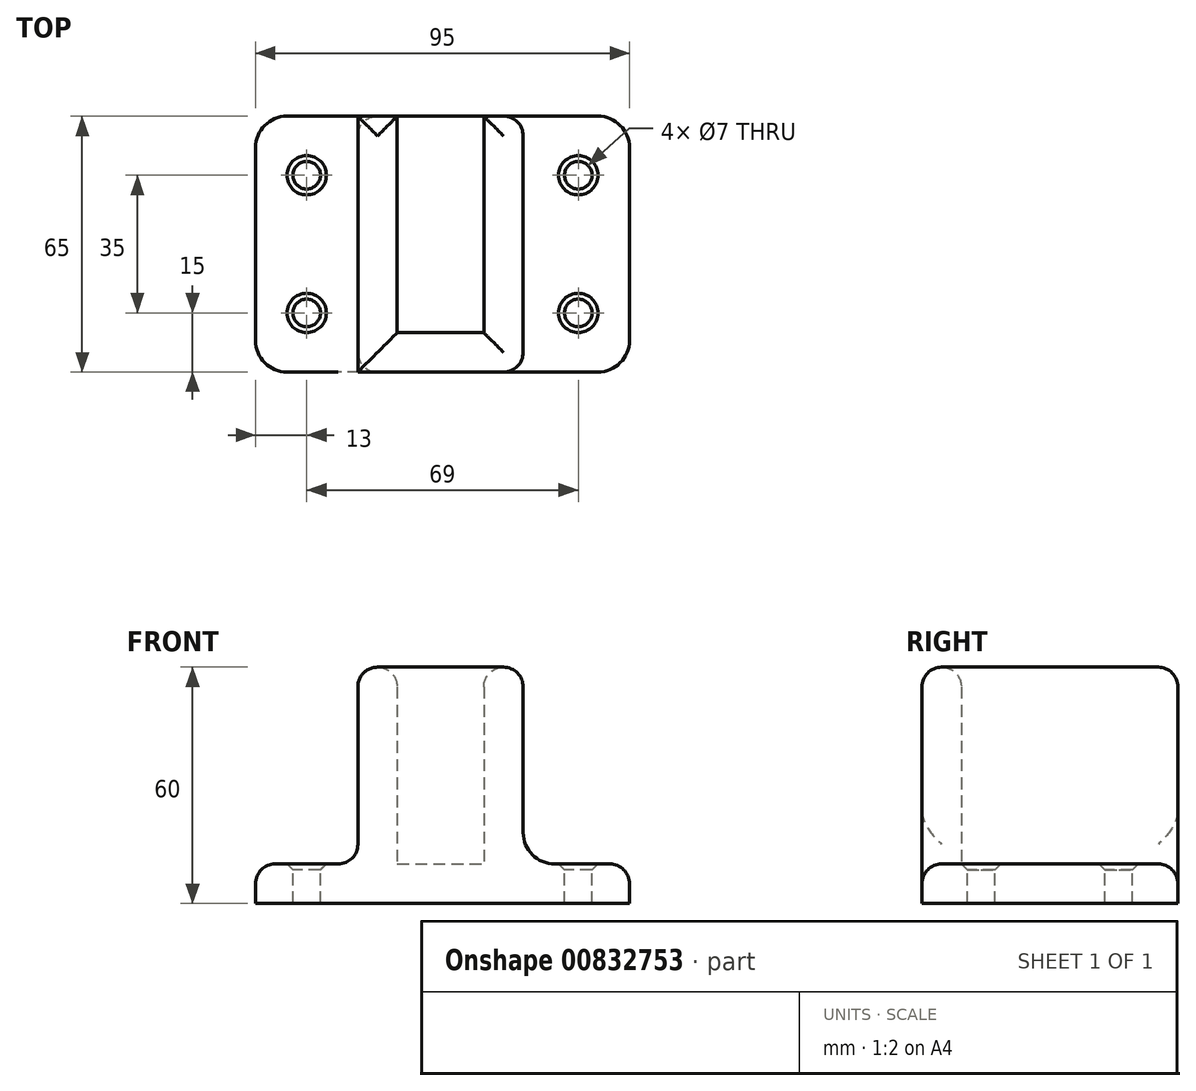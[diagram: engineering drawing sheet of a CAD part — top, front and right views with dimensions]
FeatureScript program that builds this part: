
annotation { "Feature Type Name" : "Feature", "Feature Type Description" : "" }
export const myFeature = defineFeature(function(context is Context, id is Id, definition is map)
    precondition{}
    {
        {
            var Q0;
            Q0=qCreatedBy(makeId("Top.planeOp"),FACE);
            var sketch = newSketch(context, id + "F0", { "sketchPlane" : qUnion([Q0])});
            skLineSegment(sketch, "E0.bottom", {"start": v(0, 0) * mm, "end": v(95, 0) * mm});
            skLineSegment(sketch, "E0.top", {"start": v(0, 65) * mm, "end": v(95, 65) * mm});
            skLineSegment(sketch, "E0.left", {"start": v(0, 0) * mm, "end": v(0, 65) * mm});
            skLineSegment(sketch, "E0.right", {"start": v(95, 0) * mm, "end": v(95, 65) * mm});
            skSolve(sketch);
        }
        {
            var Q0;
            Q0 = qSketchRegion(id + "F0", true);
            extrude(context, id + "F1", {"entities" : qUnion([Q0]), "depth" : 10 * mm, "offsetDistance" : 25 * mm});
        }
        {
            var Q0;
            Q0=makeQuery(id+"F1.opExtrude","CAP_FACE",FACE,{"disambiguationData":[OSD([sQuery(id+"F0.wireOp",EDGE,"E0.bottom"),sQuery(id+"F0.wireOp",EDGE,"E0.top"),sQuery(id+"F0.wireOp",EDGE,"E0.left"),sQuery(id+"F0.wireOp",EDGE,"E0.right")])],"isStart":false});
            var sketch = newSketch(context, id + "F2", { "sketchPlane" : qUnion([Q0])});
            skLineSegment(sketch, "E1.bottom", {"start": v(26, 65) * mm, "end": v(36, 65) * mm});
            skLineSegment(sketch, "E1.top", {"start": v(26, 0) * mm, "end": v(68, 0) * mm});
            skLineSegment(sketch, "E1.left", {"start": v(26, 65) * mm, "end": v(26, 0) * mm});
            skLineSegment(sketch, "E1.right", {"start": v(68, 65) * mm, "end": v(68, 0) * mm});
            skLineSegment(sketch, "E2.top", {"start": v(36, 10) * mm, "end": v(58, 10) * mm});
            skLineSegment(sketch, "E2.left", {"start": v(36, 65) * mm, "end": v(36, 10) * mm});
            skLineSegment(sketch, "E2.right", {"start": v(58, 65) * mm, "end": v(58, 10) * mm});
            skLineSegment(sketch, "E3.trimOffspring", {"start": v(58, 65) * mm, "end": v(68, 65) * mm});
            skSolve(sketch);
        }
        {
            var Q0;
            Q0 = qSketchRegion(id + "F2", true);
            extrude(context, id + "F3", {"entities" : qUnion([Q0]), "operationType" : NewBodyOperationType.ADD, "depth" : 50 * mm, "offsetDistance" : 25 * mm});
        }
        {
            var Q0;
            Q0=makeQuery(id+"F3.opExtrude","CAP_EDGE",EDGE,{"disambiguationData":[OSD([sQuery(id+"F2.wireOp",EDGE,"E1.right")])],"isStart":true});
            var Q1;
            Q1=makeQuery(id+"F3.opExtrude","CAP_EDGE",EDGE,{"disambiguationData":[OSD([sQuery(id+"F2.wireOp",EDGE,"E1.left")])],"isStart":true});
            fillet(context, id + "F4", {"entities" : qUnion([Q0, Q1]), "radius" : 8 * mm, "tangentPropagation" : true, "allowEdgeOverflow" : false});
        }
        {
            var Q0;
            {var subQ0=sQuery(id+"F0.wireOp",EDGE,"E0.top");var subQ1=sQuery(id+"F0.wireOp",EDGE,"E0.right");var subQ2=sQuery(id+"F0.wireOp",EDGE,"E0.bottom");Q0=makeQuery(id+"F3.boolean.opBoolean","SPLIT",FACE,{"disambiguationData":[TD([makeQuery(id+"F1.opExtrude","SWEPT_FACE",FACE,{"disambiguationData":[OSD([subQ1])]})])],"derivedFrom":makeQuery(id+"F1.opExtrude","CAP_FACE",FACE,{"disambiguationData":[OSD([subQ2,subQ0,sQuery(id+"F0.wireOp",EDGE,"E0.left"),subQ1])],"isStart":false})});}
            var Q1;
            {var subQ0=sQuery(id+"F0.wireOp",EDGE,"E0.left");var subQ1=sQuery(id+"F0.wireOp",EDGE,"E0.top");var subQ2=sQuery(id+"F0.wireOp",EDGE,"E0.bottom");Q1=makeQuery(id+"F3.boolean.opBoolean","SPLIT",FACE,{"disambiguationData":[TD([makeQuery(id+"F1.opExtrude","SWEPT_FACE",FACE,{"disambiguationData":[OSD([subQ0])]})])],"derivedFrom":makeQuery(id+"F1.opExtrude","CAP_FACE",FACE,{"disambiguationData":[OSD([subQ2,subQ1,subQ0,sQuery(id+"F0.wireOp",EDGE,"E0.right")])],"isStart":false})});}
            var Q2;
            Q2=makeQuery(id+"F3.opExtrude","CAP_FACE",FACE,{"disambiguationData":[OSD([sQuery(id+"F2.wireOp",EDGE,"E1.bottom"),sQuery(id+"F2.wireOp",EDGE,"E1.top"),sQuery(id+"F2.wireOp",EDGE,"E1.left"),sQuery(id+"F2.wireOp",EDGE,"E1.right"),sQuery(id+"F2.wireOp",EDGE,"E2.top"),sQuery(id+"F2.wireOp",EDGE,"E2.left"),sQuery(id+"F2.wireOp",EDGE,"E2.right"),sQuery(id+"F2.wireOp",EDGE,"E3.trimOffspring")])],"isStart":false});
            fillet(context, id + "F5", {"entities" : qUnion([Q0, Q1, Q2]), "radius" : 5 * mm, "tangentPropagation" : true, "allowEdgeOverflow" : false});
        }
        {
            var Q0;
            {var subQ0=sQuery(id+"F0.wireOp",EDGE,"E0.left");var subQ1=sQuery(id+"F0.wireOp",EDGE,"E0.top");var subQ2=sQuery(id+"F0.wireOp",EDGE,"E0.bottom");Q0=makeQuery(id+"F3.boolean.opBoolean","SPLIT",FACE,{"disambiguationData":[TD([makeQuery(id+"F1.opExtrude","SWEPT_FACE",FACE,{"disambiguationData":[OSD([subQ0])]})])],"derivedFrom":makeQuery(id+"F1.opExtrude","CAP_FACE",FACE,{"disambiguationData":[OSD([subQ2,subQ1,subQ0,sQuery(id+"F0.wireOp",EDGE,"E0.right")])],"isStart":false})});}
            var sketch = newSketch(context, id + "F6", { "sketchPlane" : qUnion([Q0])});
            skPoint(sketch, "E4", {"position": v(13, 50) * mm});
            skPoint(sketch, "E5", {"position": v(13, 15) * mm});
            skPoint(sketch, "E6", {"position": v(82, 50) * mm});
            skPoint(sketch, "E7", {"position": v(82, 15) * mm});
            skSolve(sketch);
        }
        {
            var Q0;
            Q0=sQuery(id+"F6.wireOp",VERTEX,"E4");
            var Q1;
            Q1=sQuery(id+"F6.wireOp",VERTEX,"E5");
            var Q2;
            Q2=sQuery(id+"F6.wireOp",VERTEX,"E6");
            var Q3;
            Q3=sQuery(id+"F6.wireOp",VERTEX,"E7");
            var Q4;
            Q4=makeQuery(id+"F1.opExtrude","SWEPT_BODY",BODY,{"disambiguationData":[OSD([sQuery(id+"F0.wireOp",EDGE,"E0.bottom"),sQuery(id+"F0.wireOp",EDGE,"E0.top"),sQuery(id+"F0.wireOp",EDGE,"E0.left"),sQuery(id+"F0.wireOp",EDGE,"E0.right")])]});
            hole(context, id + "F7", {"style" : HoleStyle.C_SINK, "endStyle" : HoleEndStyle.THROUGH, "holeDiameter" : 7 * mm, "cSinkDiameter" : 10 * mm, "cSinkAngle" : 90 * degree, "majorDiameter" : 5 * mm, "isTappedThrough" : true, "tappedDepth" : 12 * mm, "tapClearance" : 3, "locations" : qUnion([Q0, Q1, Q2, Q3]), "scope" : qUnion([Q4])});
        }
        {
            var Q0;
            Q0=makeQuery(id+"F1.opExtrude","SWEPT_EDGE",EDGE,{"disambiguationData":[OSD([sQuery(id+"F0.wireOp",EDGE,"E0.top"),sQuery(id+"F0.wireOp",EDGE,"E0.left")])]});
            var Q1;
            Q1=makeQuery(id+"F1.opExtrude","SWEPT_EDGE",EDGE,{"disambiguationData":[OSD([sQuery(id+"F0.wireOp",EDGE,"E0.top"),sQuery(id+"F0.wireOp",EDGE,"E0.right")])]});
            var Q2;
            Q2=makeQuery(id+"F1.opExtrude","SWEPT_EDGE",EDGE,{"disambiguationData":[OSD([sQuery(id+"F0.wireOp",EDGE,"E0.bottom"),sQuery(id+"F0.wireOp",EDGE,"E0.right")])]});
            var Q3;
            Q3=makeQuery(id+"F1.opExtrude","SWEPT_EDGE",EDGE,{"disambiguationData":[OSD([sQuery(id+"F0.wireOp",EDGE,"E0.bottom"),sQuery(id+"F0.wireOp",EDGE,"E0.left")])]});
            fillet(context, id + "F8", {"entities" : qUnion([Q0, Q1, Q2, Q3]), "radius" : 8 * mm, "tangentPropagation" : true, "allowEdgeOverflow" : false});
        }
    });
